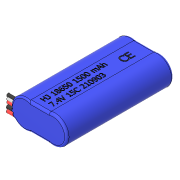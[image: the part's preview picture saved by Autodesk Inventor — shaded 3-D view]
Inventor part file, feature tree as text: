
AUTODESK INVENTOR PART (.ipt)
format: ipt  version: 2019.5 (Build 235369000, 369)  size: 992,256 bytes
history: native  units: mm
features: extrude x4, sketch x4, fillet x2, projected_geometry x1
ambient origin geometry x8: Origin, YZ Plane, XZ Plane, XY Plane, X Axis, Y Axis, Z Axis, Center Point
bodies: Solid1 (feature_tree)
feature tree (11):
  extrude  "Extrusion1"  Depth=18.0mm
  extrude  "Extrusion2"  Depth=72.0mm TaperAngle=0.0deg
  extrude  "Extrusion3"  Depth=4.5mm
  fillet  "Fillet1"  Radius=22.0mm
  fillet  "Fillet2"  Radius=2.0mm
  extrude  "Extrusion4"  Depth=22.0mm TaperAngle=0.0deg
  sketch  "Sketch1"  dims[d0=18.75mm d1=18.0mm]
  sketch  "Sketch2"  dims[d2=9.0mm d3=72.0mm d4=0.0mm]
  sketch  "Sketch3"  dims[d5=2.5mm d6=4.5mm d7=22.0mm d8=0.0mm d9=2.0mm]
  projected_geometry  "Projected Loop1"
  sketch  "Sketch4"  dims[d11=0.5mm d12=22.0mm d13=0.0mm d14=1.5mm d15=1.0mm d16=0.1mm d17=0.0mm]
